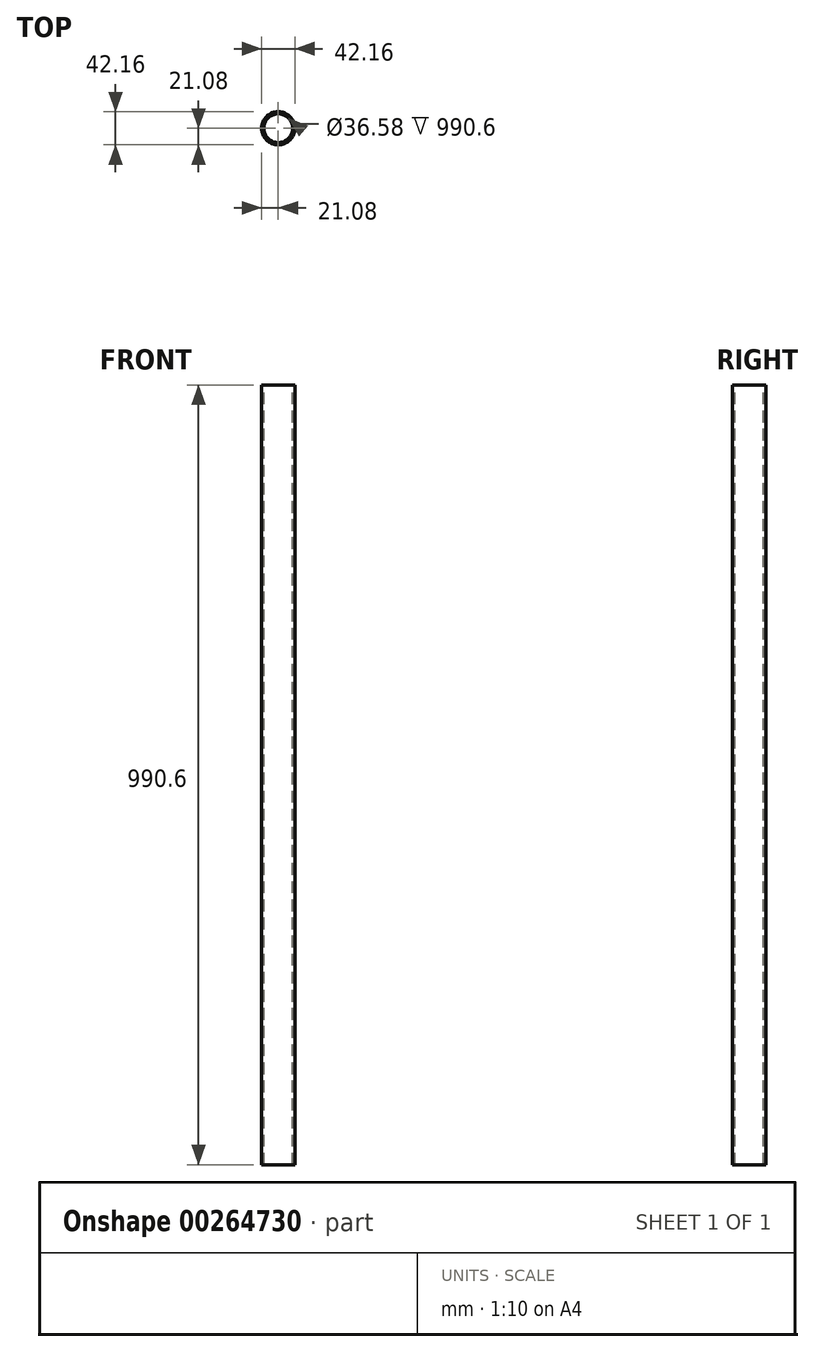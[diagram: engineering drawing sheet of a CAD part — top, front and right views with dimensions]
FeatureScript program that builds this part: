
annotation { "Feature Type Name" : "Feature", "Feature Type Description" : "" }
export const myFeature = defineFeature(function(context is Context, id is Id, definition is map)
    precondition{}
    {
        {
            var Q0;
            Q0=qCreatedBy(makeId("Top.planeOp"),FACE);
            var sketch = newSketch(context, id + "F0", { "sketchPlane" : qUnion([Q0])});
            skCircle(sketch, "E0", {"center": v(0, 0) * mm, "radius": 21.08 * mm});
            skCircle(sketch, "E1.0", {"center": v(0, 0) * mm, "radius": 18.29 * mm});
            skSolve(sketch);
        }
        {
            var Q0;
            Q0=qCreatedBy(makeId("Front.planeOp"),FACE);
            var sketch = newSketch(context, id + "F1", { "sketchPlane" : qUnion([Q0])});
            skLineSegment(sketch, "E2", {"start": v(0, 0) * mm, "end": v(0, 990.6) * mm});
            skSolve(sketch);
        }
        {
            var Q0;
            Q0=makeQuery(id+"F0.imprint","IMPRINT",FACE,{"disambiguationData":[TD([[makeQuery(id+"F0.imprint","IMPRINT",EDGE,{"derivedFrom":sQuery(id+"F0.wireOp",EDGE,"E0")}),1.0]])]});
            var Q1;
            Q1=sQuery(id+"F1.wireOp",EDGE,"E2");
            sweep(context, id + "F2", {"profiles" : qUnion([Q0]), "path" : qUnion([Q1])});
        }
    });
